# Revit family: LSP-2G
name_source: partatom
category: Lighting Fixtures
revit_build: Autodesk Revit 2018 (Build: 20181015_0930(x64)
units: mm (PartAtom-declared; Revit-internal decimal feet)

## family parameters
Always vertical = Yes
Cut with Voids When Loaded = No
Host = Ceiling
Light Source = Yes
OmniClass Number = 23.80.70.11
OmniClass Title = Luminaries for Internal Lighting
Part Type = Normal
Room Calculation Point = No
Round Connector Dimension = Use Diameter
Shared = No

## types (5) — shared parameters
Color Filter = 16777215
Dimming Lamp Color Temperature Shift = <None>
Emit Shape Visible in Rendering = No
Light Source Symbol Size = 300 mm
lsp casing = lsp casing
lsp led panel = lsp led panel
volts = 277 V

## per-type parameters (varying)
| type | Apparent Load | Emit from Rectangle Length | Emit from Rectangle Width | lenght | width |
| LSP-2G 1'X4' 30W | 30 VA | 919 mm | 85 mm | 305 mm | 1219 mm |
| LSP-2G 2'X2' 30W | 30 VA | 310 mm | 390 mm | 610 mm | 610 mm |
| LSP-2G 2'X2' 36W | 36 VA | 310 mm | 390 mm | 610 mm | 610 mm |
| LSP-2G 2'X4' 40W | 40 VA | 919 mm | 390 mm | 610 mm | 1219 mm |
| LSP-2G 2'X4' 50W | 50 VA | 919 mm | 390 mm | 610 mm | 1219 mm |

## geometry (parser evidence)
native form markers: Sweep x5
no freeform markers — native parametric forms only
